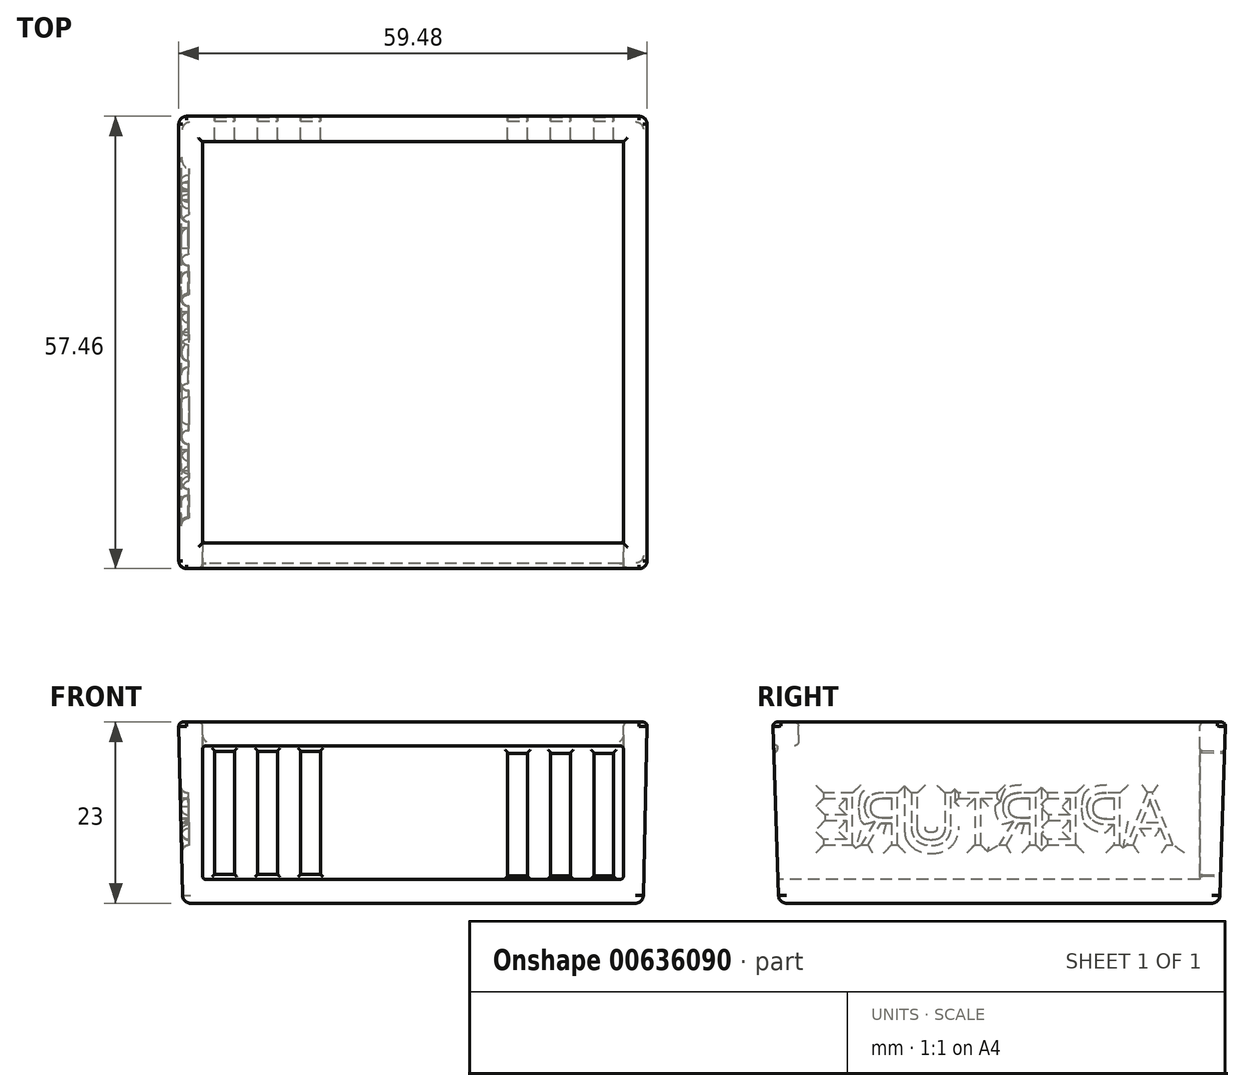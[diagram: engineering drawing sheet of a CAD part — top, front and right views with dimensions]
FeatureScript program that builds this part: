
annotation { "Feature Type Name" : "Feature", "Feature Type Description" : "" }
export const myFeature = defineFeature(function(context is Context, id is Id, definition is map)
    precondition{}
    {
        {
            var Q0;
            Q0=qCreatedBy(makeId("Top.planeOp"),FACE);
            var sketch = newSketch(context, id + "F0", { "sketchPlane" : qUnion([Q0])});
            skLineSegment(sketch, "E0.bottom", {"start": v(29.25, 28) * mm, "end": v(-29.25, 28) * mm});
            skLineSegment(sketch, "E0.top", {"start": v(29.25, -28) * mm, "end": v(-29.25, -28) * mm});
            skLineSegment(sketch, "E0.left", {"start": v(29.25, 28) * mm, "end": v(29.25, -28) * mm});
            skLineSegment(sketch, "E0.right", {"start": v(-29.25, 28) * mm, "end": v(-29.25, -28) * mm});
            skPoint(sketch, "E0.middle", {"position": v(0, 0) * mm});
            skSolve(sketch);
        }
        {
            var Q0;
            Q0=qCreatedBy(makeId("Top.planeOp"),FACE);
            cPlane(context, id + "F1", {"entities" : qUnion([Q0]), "cplaneType" : CPlaneType.OFFSET, "offset" : 23 * mm, "width" : 150 * mm, "height" : 150 * mm});
        }
        {
            var Q0;
            Q0=qCreatedBy(id+"F1.planeOp",FACE);
            var sketch = newSketch(context, id + "F2", { "sketchPlane" : qUnion([Q0])});
            skLineSegment(sketch, "E1.bottom", {"start": v(29.75, 28.75) * mm, "end": v(-29.75, 28.75) * mm});
            skLineSegment(sketch, "E1.top", {"start": v(29.75, -28.75) * mm, "end": v(-29.75, -28.75) * mm});
            skLineSegment(sketch, "E1.left", {"start": v(29.75, 28.75) * mm, "end": v(29.75, -28.75) * mm});
            skLineSegment(sketch, "E1.right", {"start": v(-29.75, 28.75) * mm, "end": v(-29.75, -28.75) * mm});
            skPoint(sketch, "E1.middle", {"position": v(0, 0) * mm});
            skSolve(sketch);
        }
        {
            var Q0;
            Q0=makeQuery(id+"F0.imprint","IMPRINT",FACE,{"disambiguationData":[TD([[makeQuery(id+"F0.imprint","IMPRINT",EDGE,{"derivedFrom":sQuery(id+"F0.wireOp",EDGE,"E0.bottom")}),1.0]])]});
            var Q1;
            Q1=makeQuery(id+"F2.imprint","IMPRINT",FACE,{"disambiguationData":[TD([[makeQuery(id+"F2.imprint","IMPRINT",EDGE,{"derivedFrom":sQuery(id+"F2.wireOp",EDGE,"E1.bottom")}),1.0]])]});
            loft(context, id + "F3", {"sheetProfilesArray" : [{ "sheetProfileEntities" : qUnion([Q0]) }, { "sheetProfileEntities" : qUnion([Q1]) }]});
        }
        {
            var Q0;
            Q0=qCreatedBy(id+"F1.planeOp",FACE);
            var sketch = newSketch(context, id + "F4", { "sketchPlane" : qUnion([Q0])});
            skLineSegment(sketch, "E2.bottom", {"start": v(26.75, 25.5) * mm, "end": v(-26.75, 25.5) * mm});
            skLineSegment(sketch, "E2.top", {"start": v(26.75, -25.5) * mm, "end": v(-26.75, -25.5) * mm});
            skLineSegment(sketch, "E2.left", {"start": v(26.75, 25.5) * mm, "end": v(26.75, -25.5) * mm});
            skLineSegment(sketch, "E2.right", {"start": v(-26.75, 25.5) * mm, "end": v(-26.75, -25.5) * mm});
            skPoint(sketch, "E2.middle", {"position": v(0, 0) * mm});
            skSolve(sketch);
        }
        {
            var Q0;
            Q0=makeQuery(id+"F4.imprint","IMPRINT",FACE,{"disambiguationData":[TD([[makeQuery(id+"F4.imprint","IMPRINT",EDGE,{"derivedFrom":sQuery(id+"F4.wireOp",EDGE,"E2.bottom")}),1.0]])]});
            extrude(context, id + "F5", {"entities" : qUnion([Q0]), "operationType" : NewBodyOperationType.REMOVE, "oppositeDirection" : true, "depth" : 20 * mm, "offsetDistance" : 25 * mm});
        }
        {
            var Q0;
            Q0=makeQuery(id+"F3.opLoft","SWEPT_FACE",FACE,{"disambiguationData":[OSD([sQuery(id+"F0.wireOp",EDGE,"E0.bottom"),sQuery(id+"F0.wireOp",EDGE,"E0.left"),sQuery(id+"F0.wireOp",EDGE,"E0.right"),sQuery(id+"F2.wireOp",EDGE,"E1.bottom"),sQuery(id+"F2.wireOp",EDGE,"E1.left"),sQuery(id+"F2.wireOp",EDGE,"E1.right")])]});
            cPlane(context, id + "F6", {"entities" : qUnion([Q0]), "cplaneType" : CPlaneType.OFFSET, "offset" : 0 * mm, "width" : 150 * mm, "height" : 150 * mm});
        }
        {
            var Q0;
            Q0=qCreatedBy(id+"F6.planeOp",FACE);
            var sketch = newSketch(context, id + "F7", { "sketchPlane" : qUnion([Q0])});
            skLineSegment(sketch, "E3.bottom", {"start": v(-22.97, 19.97) * mm, "end": v(-25.49, 19.97) * mm});
            skLineSegment(sketch, "E3.top", {"start": v(-22.97, 4.28) * mm, "end": v(-25.49, 4.28) * mm});
            skLineSegment(sketch, "E3.left", {"start": v(-22.97, 19.97) * mm, "end": v(-22.97, 4.28) * mm});
            skLineSegment(sketch, "E3.right", {"start": v(-25.49, 19.97) * mm, "end": v(-25.49, 4.28) * mm});
            skPoint(sketch, "E3.middle", {"position": v(-24.23, 12.13) * mm});
            skLineSegment(sketch, "E4.bottom", {"start": v(-17.5, 19.97) * mm, "end": v(-20.03, 19.97) * mm});
            skLineSegment(sketch, "E4.top", {"start": v(-17.5, 4.28) * mm, "end": v(-20.03, 4.28) * mm});
            skLineSegment(sketch, "E4.left", {"start": v(-17.5, 19.97) * mm, "end": v(-17.5, 4.28) * mm});
            skLineSegment(sketch, "E4.right", {"start": v(-20.03, 19.97) * mm, "end": v(-20.03, 4.28) * mm});
            skPoint(sketch, "E4.middle", {"position": v(-18.76, 12.13) * mm});
            skLineSegment(sketch, "E5.bottom", {"start": v(-12.04, 19.97) * mm, "end": v(-14.56, 19.97) * mm});
            skLineSegment(sketch, "E5.top", {"start": v(-12.04, 4.28) * mm, "end": v(-14.56, 4.28) * mm});
            skLineSegment(sketch, "E5.left", {"start": v(-12.04, 19.97) * mm, "end": v(-12.04, 4.28) * mm});
            skLineSegment(sketch, "E5.right", {"start": v(-14.56, 19.97) * mm, "end": v(-14.56, 4.28) * mm});
            skPoint(sketch, "E5.middle", {"position": v(-13.3, 12.13) * mm});
            skLineSegment(sketch, "E6.bottom", {"start": v(14.27, 20.2) * mm, "end": v(11.75, 20.2) * mm});
            skLineSegment(sketch, "E6.top", {"start": v(14.27, 4.5) * mm, "end": v(11.75, 4.5) * mm});
            skLineSegment(sketch, "E6.left", {"start": v(14.27, 20.2) * mm, "end": v(14.27, 4.5) * mm});
            skLineSegment(sketch, "E6.right", {"start": v(11.75, 20.2) * mm, "end": v(11.75, 4.5) * mm});
            skPoint(sketch, "E6.middle", {"position": v(13, 12.36) * mm});
            skLineSegment(sketch, "E7.bottom", {"start": v(19.73, 20.2) * mm, "end": v(17.21, 20.2) * mm});
            skLineSegment(sketch, "E7.top", {"start": v(19.73, 4.5) * mm, "end": v(17.21, 4.5) * mm});
            skLineSegment(sketch, "E7.left", {"start": v(19.73, 20.2) * mm, "end": v(19.73, 4.5) * mm});
            skLineSegment(sketch, "E7.right", {"start": v(17.21, 20.2) * mm, "end": v(17.21, 4.5) * mm});
            skPoint(sketch, "E7.middle", {"position": v(18.47, 12.36) * mm});
            skLineSegment(sketch, "E8.bottom", {"start": v(25.2, 20.2) * mm, "end": v(22.67, 20.2) * mm});
            skLineSegment(sketch, "E8.top", {"start": v(25.2, 4.5) * mm, "end": v(22.67, 4.5) * mm});
            skLineSegment(sketch, "E8.left", {"start": v(25.2, 20.2) * mm, "end": v(25.2, 4.5) * mm});
            skLineSegment(sketch, "E8.right", {"start": v(22.67, 20.2) * mm, "end": v(22.67, 4.5) * mm});
            skPoint(sketch, "E8.middle", {"position": v(23.94, 12.36) * mm});
            skSolve(sketch);
        }
        {
            var Q0;
            Q0 = qSketchRegion(id + "F7", true);
            extrude(context, id + "F8", {"entities" : qUnion([Q0]), "operationType" : NewBodyOperationType.REMOVE, "oppositeDirection" : true, "depth" : 5 * mm, "offsetDistance" : 25 * mm});
        }
        {
            var Q0;
            Q0=makeQuery(id+"F5.boolean.opBoolean","COPY",FACE,{"derivedFrom":makeQuery(id+"F5.opExtrude","SWEPT_FACE",FACE,{"disambiguationData":[OSD([sQuery(id+"F4.wireOp",EDGE,"E2.top")])]})});
            var sketch = newSketch(context, id + "F9", { "sketchPlane" : qUnion([Q0])});
            skPoint(sketch, "E9", {"position": v(-26.75, 20) * mm});
            skPoint(sketch, "E10", {"position": v(26.75, 20) * mm});
            skPoint(sketch, "E11", {"position": v(26.75, 3) * mm});
            skPoint(sketch, "E12", {"position": v(-26.75, 3) * mm});
            skLineSegment(sketch, "E13", {"start": v(-26.75, 20) * mm, "end": v(-26.75, 3) * mm});
            skLineSegment(sketch, "E14", {"start": v(-26.75, 20) * mm, "end": v(26.75, 20) * mm});
            skLineSegment(sketch, "E15", {"start": v(26.75, 20) * mm, "end": v(26.75, 3) * mm});
            skLineSegment(sketch, "E16", {"start": v(26.75, 3) * mm, "end": v(-26.75, 3) * mm});
            skSolve(sketch);
        }
        {
            var Q0;
            Q0=makeQuery(id+"F9.imprint","IMPRINT",FACE,{"disambiguationData":[TD([[makeQuery(id+"F9.imprint","IMPRINT",EDGE,{"derivedFrom":sQuery(id+"F9.wireOp",EDGE,"E13")}),-1.0]])]});
            extrude(context, id + "F10", {"entities" : qUnion([Q0]), "operationType" : NewBodyOperationType.REMOVE, "oppositeDirection" : true, "depth" : 25 * mm, "offsetDistance" : 25 * mm});
        }
        {
            var Q0;
            Q0=makeQuery(id+"F3.opLoft","SWEPT_FACE",FACE,{"disambiguationData":[OSD([sQuery(id+"F0.wireOp",EDGE,"E0.bottom"),sQuery(id+"F0.wireOp",EDGE,"E0.top"),sQuery(id+"F0.wireOp",EDGE,"E0.right"),sQuery(id+"F2.wireOp",EDGE,"E1.bottom"),sQuery(id+"F2.wireOp",EDGE,"E1.top"),sQuery(id+"F2.wireOp",EDGE,"E1.right")])]});
            var sketch = newSketch(context, id + "F11", { "sketchPlane" : qUnion([Q0])});
            skText(sketch, "E17", { "text": "APERTURE\n", "fontName": "OpenSans-Regular.ttf"});
            const initialGuessF11  = {"E17": [-0.02208, 0.00804, 1, 0, 0.00665]};
            skSetInitialGuess(sketch, initialGuessF11);
            skSolve(sketch);
        }
        {
            var Q0;
            Q0 = qSketchRegion(id + "F11", true);
            extrude(context, id + "F12", {"entities" : qUnion([Q0]), "operationType" : NewBodyOperationType.REMOVE, "oppositeDirection" : true, "depth" : 1 * mm, "offsetDistance" : 25 * mm});
        }
        {
            var Q0;
            Q0=makeQuery(id+"F10.boolean.opBoolean","MERGE",EDGE,{"derivedFrom":[makeQuery(id+"F5.boolean.opBoolean","COPY",EDGE,{"derivedFrom":makeQuery(id+"F5.opExtrude","CAP_EDGE",EDGE,{"disambiguationData":[OSD([sQuery(id+"F4.wireOp",EDGE,"E2.right")])],"isStart":false})}),makeQuery(id+"F10.opExtrude","SWEPT_EDGE",EDGE,{"disambiguationData":[OSD([sQuery(id+"F9.wireOp",EDGE,"E15"),sQuery(id+"F9.wireOp",EDGE,"E16")])]})]});
            var Q1;
            Q1=makeQuery(id+"F10.boolean.opBoolean","INTERSECT",EDGE,{"derivedFrom":[makeQuery(id+"F3.opLoft","SWEPT_FACE",FACE,{"disambiguationData":[OSD([sQuery(id+"F0.wireOp",EDGE,"E0.top"),sQuery(id+"F0.wireOp",EDGE,"E0.left"),sQuery(id+"F0.wireOp",EDGE,"E0.right"),sQuery(id+"F2.wireOp",EDGE,"E1.top"),sQuery(id+"F2.wireOp",EDGE,"E1.left"),sQuery(id+"F2.wireOp",EDGE,"E1.right")])]}),makeQuery(id+"F10.opExtrude","SWEPT_FACE",FACE,{"disambiguationData":[OSD([sQuery(id+"F9.wireOp",EDGE,"E14")])]})]});
            var Q2;
            Q2=makeQuery(id+"F10.boolean.opBoolean","COPY",FACE,{"derivedFrom":makeQuery(id+"F10.opExtrude","SWEPT_FACE",FACE,{"disambiguationData":[OSD([sQuery(id+"F9.wireOp",EDGE,"E14")])]})});
            var Q3;
            Q3=makeQuery(id+"F3.opLoft","CAP_FACE",FACE,{"disambiguationData":[OSD([makeQuery(id+"F2.imprint","IMPRINT",FACE,{"disambiguationData":[TD([[makeQuery(id+"F2.imprint","IMPRINT",EDGE,{"derivedFrom":sQuery(id+"F2.wireOp",EDGE,"E1.bottom")}),1.0]])]})])],"isStart":true});
            fillet(context, id + "F13", {"entities" : qUnion([Q0, Q1, Q2, Q3]), "radius" : .5 * mm, "tangentPropagation" : true, "allowEdgeOverflow" : false});
        }
        {
            var Q0;
            Q0=makeQuery(id+"F3.opLoft","CAP_FACE",FACE,{"disambiguationData":[OSD([makeQuery(id+"F0.imprint","IMPRINT",FACE,{"disambiguationData":[TD([[makeQuery(id+"F0.imprint","IMPRINT",EDGE,{"derivedFrom":sQuery(id+"F0.wireOp",EDGE,"E0.bottom")}),1.0]])]})])],"isStart":true});
            var Q1;
            Q1=makeQuery(id+"F3.opLoft","SWEPT_FACE",FACE,{"disambiguationData":[OSD([sQuery(id+"F0.wireOp",EDGE,"E0.bottom"),sQuery(id+"F0.wireOp",EDGE,"E0.top"),sQuery(id+"F0.wireOp",EDGE,"E0.left"),sQuery(id+"F2.wireOp",EDGE,"E1.bottom"),sQuery(id+"F2.wireOp",EDGE,"E1.top"),sQuery(id+"F2.wireOp",EDGE,"E1.left")])]});
            var Q2;
            {var subQ0=sQuery(id+"F2.wireOp",EDGE,"E1.right");var subQ2=sQuery(id+"F2.wireOp",EDGE,"E1.bottom");var subQ3=sQuery(id+"F0.wireOp",EDGE,"E0.right");var subQ5=sQuery(id+"F0.wireOp",EDGE,"E0.bottom");var subQ6=sQuery(id+"F2.wireOp",EDGE,"E1.top");var subQ7=sQuery(id+"F0.wireOp",EDGE,"E0.top");Q2=makeQuery(id+"F12.boolean.opBoolean","SPLIT",FACE,{"disambiguationData":[TD([makeQuery(id+"F12.opExtrude","SWEPT_FACE",FACE,{"disambiguationData":[OSD([sQuery(id+"F11.wireOp",EDGE,"E17.sketch_text.stroke-0")])]})])],"derivedFrom":makeQuery(id+"F3.opLoft","SWEPT_FACE",FACE,{"disambiguationData":[OSD([subQ5,subQ7,subQ3,subQ2,subQ6,subQ0])]})});}
            fillet(context, id + "F14", {"entities" : qUnion([Q0, Q1, Q2]), "radius" : 1 * mm, "tangentPropagation" : true, "allowEdgeOverflow" : false});
        }
        {
            var Q0;
            Q0=makeQuery(id+"F8.boolean.opBoolean","INTERSECT",EDGE,{"derivedFrom":[makeQuery(id+"F5.boolean.opBoolean","COPY",FACE,{"derivedFrom":makeQuery(id+"F5.opExtrude","SWEPT_FACE",FACE,{"disambiguationData":[OSD([sQuery(id+"F4.wireOp",EDGE,"E2.bottom")])]})}),makeQuery(id+"F8.opExtrude","SWEPT_FACE",FACE,{"disambiguationData":[OSD([sQuery(id+"F7.wireOp",EDGE,"E3.right")])]})]});
            var Q1;
            Q1=makeQuery(id+"F8.boolean.opBoolean","COPY",EDGE,{"derivedFrom":makeQuery(id+"F8.opExtrude","CAP_EDGE",EDGE,{"disambiguationData":[OSD([sQuery(id+"F7.wireOp",EDGE,"E3.right")])],"isStart":true})});
            var Q2;
            Q2=makeQuery(id+"F8.boolean.opBoolean","INTERSECT",EDGE,{"derivedFrom":[makeQuery(id+"F5.boolean.opBoolean","COPY",FACE,{"derivedFrom":makeQuery(id+"F5.opExtrude","SWEPT_FACE",FACE,{"disambiguationData":[OSD([sQuery(id+"F4.wireOp",EDGE,"E2.bottom")])]})}),makeQuery(id+"F8.opExtrude","SWEPT_FACE",FACE,{"disambiguationData":[OSD([sQuery(id+"F7.wireOp",EDGE,"E3.top")])]})]});
            var Q3;
            Q3=makeQuery(id+"F8.boolean.opBoolean","COPY",EDGE,{"derivedFrom":makeQuery(id+"F8.opExtrude","CAP_EDGE",EDGE,{"disambiguationData":[OSD([sQuery(id+"F7.wireOp",EDGE,"E3.top")])],"isStart":true})});
            var Q4;
            Q4=makeQuery(id+"F8.boolean.opBoolean","COPY",EDGE,{"derivedFrom":makeQuery(id+"F8.opExtrude","CAP_EDGE",EDGE,{"disambiguationData":[OSD([sQuery(id+"F7.wireOp",EDGE,"E3.left")])],"isStart":true})});
            var Q5;
            Q5=makeQuery(id+"F8.boolean.opBoolean","INTERSECT",EDGE,{"derivedFrom":[makeQuery(id+"F5.boolean.opBoolean","COPY",FACE,{"derivedFrom":makeQuery(id+"F5.opExtrude","SWEPT_FACE",FACE,{"disambiguationData":[OSD([sQuery(id+"F4.wireOp",EDGE,"E2.bottom")])]})}),makeQuery(id+"F8.opExtrude","SWEPT_FACE",FACE,{"disambiguationData":[OSD([sQuery(id+"F7.wireOp",EDGE,"E3.left")])]})]});
            var Q6;
            Q6=makeQuery(id+"F8.boolean.opBoolean","COPY",EDGE,{"derivedFrom":makeQuery(id+"F8.opExtrude","CAP_EDGE",EDGE,{"disambiguationData":[OSD([sQuery(id+"F7.wireOp",EDGE,"E3.bottom")])],"isStart":true})});
            var Q7;
            Q7=makeQuery(id+"F8.boolean.opBoolean","INTERSECT",EDGE,{"derivedFrom":[makeQuery(id+"F5.boolean.opBoolean","COPY",FACE,{"derivedFrom":makeQuery(id+"F5.opExtrude","SWEPT_FACE",FACE,{"disambiguationData":[OSD([sQuery(id+"F4.wireOp",EDGE,"E2.bottom")])]})}),makeQuery(id+"F8.opExtrude","SWEPT_FACE",FACE,{"disambiguationData":[OSD([sQuery(id+"F7.wireOp",EDGE,"E3.bottom")])]})]});
            var Q8;
            Q8=makeQuery(id+"F8.boolean.opBoolean","COPY",EDGE,{"derivedFrom":makeQuery(id+"F8.opExtrude","CAP_EDGE",EDGE,{"disambiguationData":[OSD([sQuery(id+"F7.wireOp",EDGE,"E4.left")])],"isStart":true})});
            var Q9;
            Q9=makeQuery(id+"F8.boolean.opBoolean","INTERSECT",EDGE,{"derivedFrom":[makeQuery(id+"F5.boolean.opBoolean","COPY",FACE,{"derivedFrom":makeQuery(id+"F5.opExtrude","SWEPT_FACE",FACE,{"disambiguationData":[OSD([sQuery(id+"F4.wireOp",EDGE,"E2.bottom")])]})}),makeQuery(id+"F8.opExtrude","SWEPT_FACE",FACE,{"disambiguationData":[OSD([sQuery(id+"F7.wireOp",EDGE,"E4.bottom")])]})]});
            var Q10;
            Q10=makeQuery(id+"F8.boolean.opBoolean","COPY",EDGE,{"derivedFrom":makeQuery(id+"F8.opExtrude","CAP_EDGE",EDGE,{"disambiguationData":[OSD([sQuery(id+"F7.wireOp",EDGE,"E4.bottom")])],"isStart":true})});
            var Q11;
            Q11=makeQuery(id+"F8.boolean.opBoolean","COPY",EDGE,{"derivedFrom":makeQuery(id+"F8.opExtrude","CAP_EDGE",EDGE,{"disambiguationData":[OSD([sQuery(id+"F7.wireOp",EDGE,"E5.bottom")])],"isStart":true})});
            var Q12;
            Q12=makeQuery(id+"F8.boolean.opBoolean","COPY",EDGE,{"derivedFrom":makeQuery(id+"F8.opExtrude","CAP_EDGE",EDGE,{"disambiguationData":[OSD([sQuery(id+"F7.wireOp",EDGE,"E5.left")])],"isStart":true})});
            var Q13;
            Q13=makeQuery(id+"F8.boolean.opBoolean","INTERSECT",EDGE,{"derivedFrom":[makeQuery(id+"F5.boolean.opBoolean","COPY",FACE,{"derivedFrom":makeQuery(id+"F5.opExtrude","SWEPT_FACE",FACE,{"disambiguationData":[OSD([sQuery(id+"F4.wireOp",EDGE,"E2.bottom")])]})}),makeQuery(id+"F8.opExtrude","SWEPT_FACE",FACE,{"disambiguationData":[OSD([sQuery(id+"F7.wireOp",EDGE,"E5.left")])]})]});
            var Q14;
            Q14=makeQuery(id+"F8.boolean.opBoolean","COPY",EDGE,{"derivedFrom":makeQuery(id+"F8.opExtrude","CAP_EDGE",EDGE,{"disambiguationData":[OSD([sQuery(id+"F7.wireOp",EDGE,"E4.right")])],"isStart":true})});
            var Q15;
            Q15=makeQuery(id+"F8.boolean.opBoolean","INTERSECT",EDGE,{"derivedFrom":[makeQuery(id+"F5.boolean.opBoolean","COPY",FACE,{"derivedFrom":makeQuery(id+"F5.opExtrude","SWEPT_FACE",FACE,{"disambiguationData":[OSD([sQuery(id+"F4.wireOp",EDGE,"E2.bottom")])]})}),makeQuery(id+"F8.opExtrude","SWEPT_FACE",FACE,{"disambiguationData":[OSD([sQuery(id+"F7.wireOp",EDGE,"E4.left")])]})]});
            var Q16;
            Q16=makeQuery(id+"F8.boolean.opBoolean","COPY",EDGE,{"derivedFrom":makeQuery(id+"F8.opExtrude","CAP_EDGE",EDGE,{"disambiguationData":[OSD([sQuery(id+"F7.wireOp",EDGE,"E4.top")])],"isStart":true})});
            var Q17;
            Q17=makeQuery(id+"F8.boolean.opBoolean","INTERSECT",EDGE,{"derivedFrom":[makeQuery(id+"F5.boolean.opBoolean","COPY",FACE,{"derivedFrom":makeQuery(id+"F5.opExtrude","SWEPT_FACE",FACE,{"disambiguationData":[OSD([sQuery(id+"F4.wireOp",EDGE,"E2.bottom")])]})}),makeQuery(id+"F8.opExtrude","SWEPT_FACE",FACE,{"disambiguationData":[OSD([sQuery(id+"F7.wireOp",EDGE,"E4.top")])]})]});
            var Q18;
            Q18=makeQuery(id+"F8.boolean.opBoolean","INTERSECT",EDGE,{"derivedFrom":[makeQuery(id+"F5.boolean.opBoolean","COPY",FACE,{"derivedFrom":makeQuery(id+"F5.opExtrude","SWEPT_FACE",FACE,{"disambiguationData":[OSD([sQuery(id+"F4.wireOp",EDGE,"E2.bottom")])]})}),makeQuery(id+"F8.opExtrude","SWEPT_FACE",FACE,{"disambiguationData":[OSD([sQuery(id+"F7.wireOp",EDGE,"E4.right")])]})]});
            var Q19;
            Q19=makeQuery(id+"F8.boolean.opBoolean","INTERSECT",EDGE,{"derivedFrom":[makeQuery(id+"F5.boolean.opBoolean","COPY",FACE,{"derivedFrom":makeQuery(id+"F5.opExtrude","SWEPT_FACE",FACE,{"disambiguationData":[OSD([sQuery(id+"F4.wireOp",EDGE,"E2.bottom")])]})}),makeQuery(id+"F8.opExtrude","SWEPT_FACE",FACE,{"disambiguationData":[OSD([sQuery(id+"F7.wireOp",EDGE,"E5.right")])]})]});
            var Q20;
            Q20=makeQuery(id+"F8.boolean.opBoolean","COPY",EDGE,{"derivedFrom":makeQuery(id+"F8.opExtrude","CAP_EDGE",EDGE,{"disambiguationData":[OSD([sQuery(id+"F7.wireOp",EDGE,"E5.right")])],"isStart":true})});
            var Q21;
            Q21=makeQuery(id+"F8.boolean.opBoolean","COPY",EDGE,{"derivedFrom":makeQuery(id+"F8.opExtrude","CAP_EDGE",EDGE,{"disambiguationData":[OSD([sQuery(id+"F7.wireOp",EDGE,"E5.top")])],"isStart":true})});
            var Q22;
            Q22=makeQuery(id+"F8.boolean.opBoolean","INTERSECT",EDGE,{"derivedFrom":[makeQuery(id+"F5.boolean.opBoolean","COPY",FACE,{"derivedFrom":makeQuery(id+"F5.opExtrude","SWEPT_FACE",FACE,{"disambiguationData":[OSD([sQuery(id+"F4.wireOp",EDGE,"E2.bottom")])]})}),makeQuery(id+"F8.opExtrude","SWEPT_FACE",FACE,{"disambiguationData":[OSD([sQuery(id+"F7.wireOp",EDGE,"E5.bottom")])]})]});
            var Q23;
            Q23=makeQuery(id+"F8.boolean.opBoolean","INTERSECT",EDGE,{"derivedFrom":[makeQuery(id+"F5.boolean.opBoolean","COPY",FACE,{"derivedFrom":makeQuery(id+"F5.opExtrude","SWEPT_FACE",FACE,{"disambiguationData":[OSD([sQuery(id+"F4.wireOp",EDGE,"E2.bottom")])]})}),makeQuery(id+"F8.opExtrude","SWEPT_FACE",FACE,{"disambiguationData":[OSD([sQuery(id+"F7.wireOp",EDGE,"E5.top")])]})]});
            var Q24;
            Q24=makeQuery(id+"F8.boolean.opBoolean","INTERSECT",EDGE,{"derivedFrom":[makeQuery(id+"F5.boolean.opBoolean","COPY",FACE,{"derivedFrom":makeQuery(id+"F5.opExtrude","SWEPT_FACE",FACE,{"disambiguationData":[OSD([sQuery(id+"F4.wireOp",EDGE,"E2.bottom")])]})}),makeQuery(id+"F8.opExtrude","SWEPT_FACE",FACE,{"disambiguationData":[OSD([sQuery(id+"F7.wireOp",EDGE,"E8.top")])]})]});
            var Q25;
            Q25=makeQuery(id+"F8.boolean.opBoolean","INTERSECT",EDGE,{"derivedFrom":[makeQuery(id+"F5.boolean.opBoolean","COPY",FACE,{"derivedFrom":makeQuery(id+"F5.opExtrude","SWEPT_FACE",FACE,{"disambiguationData":[OSD([sQuery(id+"F4.wireOp",EDGE,"E2.bottom")])]})}),makeQuery(id+"F8.opExtrude","SWEPT_FACE",FACE,{"disambiguationData":[OSD([sQuery(id+"F7.wireOp",EDGE,"E7.top")])]})]});
            var Q26;
            Q26=makeQuery(id+"F8.boolean.opBoolean","INTERSECT",EDGE,{"derivedFrom":[makeQuery(id+"F5.boolean.opBoolean","COPY",FACE,{"derivedFrom":makeQuery(id+"F5.opExtrude","SWEPT_FACE",FACE,{"disambiguationData":[OSD([sQuery(id+"F4.wireOp",EDGE,"E2.bottom")])]})}),makeQuery(id+"F8.opExtrude","SWEPT_FACE",FACE,{"disambiguationData":[OSD([sQuery(id+"F7.wireOp",EDGE,"E6.top")])]})]});
            var Q27;
            Q27=makeQuery(id+"F8.boolean.opBoolean","COPY",EDGE,{"derivedFrom":makeQuery(id+"F8.opExtrude","CAP_EDGE",EDGE,{"disambiguationData":[OSD([sQuery(id+"F7.wireOp",EDGE,"E6.top")])],"isStart":true})});
            var Q28;
            Q28=makeQuery(id+"F8.boolean.opBoolean","COPY",EDGE,{"derivedFrom":makeQuery(id+"F8.opExtrude","CAP_EDGE",EDGE,{"disambiguationData":[OSD([sQuery(id+"F7.wireOp",EDGE,"E7.top")])],"isStart":true})});
            var Q29;
            Q29=makeQuery(id+"F8.boolean.opBoolean","COPY",EDGE,{"derivedFrom":makeQuery(id+"F8.opExtrude","CAP_EDGE",EDGE,{"disambiguationData":[OSD([sQuery(id+"F7.wireOp",EDGE,"E8.top")])],"isStart":true})});
            var Q30;
            Q30=makeQuery(id+"F8.boolean.opBoolean","INTERSECT",EDGE,{"derivedFrom":[makeQuery(id+"F5.boolean.opBoolean","COPY",FACE,{"derivedFrom":makeQuery(id+"F5.opExtrude","SWEPT_FACE",FACE,{"disambiguationData":[OSD([sQuery(id+"F4.wireOp",EDGE,"E2.bottom")])]})}),makeQuery(id+"F8.opExtrude","SWEPT_FACE",FACE,{"disambiguationData":[OSD([sQuery(id+"F7.wireOp",EDGE,"E8.left")])]})]});
            var Q31;
            Q31=makeQuery(id+"F8.boolean.opBoolean","INTERSECT",EDGE,{"derivedFrom":[makeQuery(id+"F5.boolean.opBoolean","COPY",FACE,{"derivedFrom":makeQuery(id+"F5.opExtrude","SWEPT_FACE",FACE,{"disambiguationData":[OSD([sQuery(id+"F4.wireOp",EDGE,"E2.bottom")])]})}),makeQuery(id+"F8.opExtrude","SWEPT_FACE",FACE,{"disambiguationData":[OSD([sQuery(id+"F7.wireOp",EDGE,"E8.right")])]})]});
            var Q32;
            Q32=makeQuery(id+"F8.boolean.opBoolean","INTERSECT",EDGE,{"derivedFrom":[makeQuery(id+"F5.boolean.opBoolean","COPY",FACE,{"derivedFrom":makeQuery(id+"F5.opExtrude","SWEPT_FACE",FACE,{"disambiguationData":[OSD([sQuery(id+"F4.wireOp",EDGE,"E2.bottom")])]})}),makeQuery(id+"F8.opExtrude","SWEPT_FACE",FACE,{"disambiguationData":[OSD([sQuery(id+"F7.wireOp",EDGE,"E7.left")])]})]});
            var Q33;
            Q33=makeQuery(id+"F8.boolean.opBoolean","INTERSECT",EDGE,{"derivedFrom":[makeQuery(id+"F5.boolean.opBoolean","COPY",FACE,{"derivedFrom":makeQuery(id+"F5.opExtrude","SWEPT_FACE",FACE,{"disambiguationData":[OSD([sQuery(id+"F4.wireOp",EDGE,"E2.bottom")])]})}),makeQuery(id+"F8.opExtrude","SWEPT_FACE",FACE,{"disambiguationData":[OSD([sQuery(id+"F7.wireOp",EDGE,"E6.left")])]})]});
            var Q34;
            Q34=makeQuery(id+"F8.boolean.opBoolean","INTERSECT",EDGE,{"derivedFrom":[makeQuery(id+"F5.boolean.opBoolean","COPY",FACE,{"derivedFrom":makeQuery(id+"F5.opExtrude","SWEPT_FACE",FACE,{"disambiguationData":[OSD([sQuery(id+"F4.wireOp",EDGE,"E2.bottom")])]})}),makeQuery(id+"F8.opExtrude","SWEPT_FACE",FACE,{"disambiguationData":[OSD([sQuery(id+"F7.wireOp",EDGE,"E6.right")])]})]});
            var Q35;
            Q35=makeQuery(id+"F8.boolean.opBoolean","INTERSECT",EDGE,{"derivedFrom":[makeQuery(id+"F5.boolean.opBoolean","COPY",FACE,{"derivedFrom":makeQuery(id+"F5.opExtrude","SWEPT_FACE",FACE,{"disambiguationData":[OSD([sQuery(id+"F4.wireOp",EDGE,"E2.bottom")])]})}),makeQuery(id+"F8.opExtrude","SWEPT_FACE",FACE,{"disambiguationData":[OSD([sQuery(id+"F7.wireOp",EDGE,"E7.right")])]})]});
            var Q36;
            Q36=makeQuery(id+"F8.boolean.opBoolean","INTERSECT",EDGE,{"derivedFrom":[makeQuery(id+"F5.boolean.opBoolean","COPY",FACE,{"derivedFrom":makeQuery(id+"F5.opExtrude","SWEPT_FACE",FACE,{"disambiguationData":[OSD([sQuery(id+"F4.wireOp",EDGE,"E2.bottom")])]})}),makeQuery(id+"F8.opExtrude","SWEPT_FACE",FACE,{"disambiguationData":[OSD([sQuery(id+"F7.wireOp",EDGE,"E6.bottom")])]})]});
            var Q37;
            Q37=makeQuery(id+"F8.boolean.opBoolean","COPY",EDGE,{"derivedFrom":makeQuery(id+"F8.opExtrude","CAP_EDGE",EDGE,{"disambiguationData":[OSD([sQuery(id+"F7.wireOp",EDGE,"E6.bottom")])],"isStart":true})});
            var Q38;
            Q38=makeQuery(id+"F8.boolean.opBoolean","INTERSECT",EDGE,{"derivedFrom":[makeQuery(id+"F5.boolean.opBoolean","COPY",FACE,{"derivedFrom":makeQuery(id+"F5.opExtrude","SWEPT_FACE",FACE,{"disambiguationData":[OSD([sQuery(id+"F4.wireOp",EDGE,"E2.bottom")])]})}),makeQuery(id+"F8.opExtrude","SWEPT_FACE",FACE,{"disambiguationData":[OSD([sQuery(id+"F7.wireOp",EDGE,"E7.bottom")])]})]});
            var Q39;
            Q39=makeQuery(id+"F8.boolean.opBoolean","COPY",EDGE,{"derivedFrom":makeQuery(id+"F8.opExtrude","CAP_EDGE",EDGE,{"disambiguationData":[OSD([sQuery(id+"F7.wireOp",EDGE,"E7.bottom")])],"isStart":true})});
            var Q40;
            Q40=makeQuery(id+"F8.boolean.opBoolean","INTERSECT",EDGE,{"derivedFrom":[makeQuery(id+"F5.boolean.opBoolean","COPY",FACE,{"derivedFrom":makeQuery(id+"F5.opExtrude","SWEPT_FACE",FACE,{"disambiguationData":[OSD([sQuery(id+"F4.wireOp",EDGE,"E2.bottom")])]})}),makeQuery(id+"F8.opExtrude","SWEPT_FACE",FACE,{"disambiguationData":[OSD([sQuery(id+"F7.wireOp",EDGE,"E8.bottom")])]})]});
            var Q41;
            Q41=makeQuery(id+"F8.boolean.opBoolean","COPY",EDGE,{"derivedFrom":makeQuery(id+"F8.opExtrude","CAP_EDGE",EDGE,{"disambiguationData":[OSD([sQuery(id+"F7.wireOp",EDGE,"E8.bottom")])],"isStart":true})});
            var Q42;
            Q42=makeQuery(id+"F8.boolean.opBoolean","COPY",EDGE,{"derivedFrom":makeQuery(id+"F8.opExtrude","CAP_EDGE",EDGE,{"disambiguationData":[OSD([sQuery(id+"F7.wireOp",EDGE,"E6.right")])],"isStart":true})});
            var Q43;
            Q43=makeQuery(id+"F8.boolean.opBoolean","COPY",EDGE,{"derivedFrom":makeQuery(id+"F8.opExtrude","CAP_EDGE",EDGE,{"disambiguationData":[OSD([sQuery(id+"F7.wireOp",EDGE,"E6.left")])],"isStart":true})});
            var Q44;
            Q44=makeQuery(id+"F8.boolean.opBoolean","COPY",EDGE,{"derivedFrom":makeQuery(id+"F8.opExtrude","CAP_EDGE",EDGE,{"disambiguationData":[OSD([sQuery(id+"F7.wireOp",EDGE,"E8.left")])],"isStart":true})});
            var Q45;
            Q45=makeQuery(id+"F8.boolean.opBoolean","COPY",EDGE,{"derivedFrom":makeQuery(id+"F8.opExtrude","CAP_EDGE",EDGE,{"disambiguationData":[OSD([sQuery(id+"F7.wireOp",EDGE,"E7.left")])],"isStart":true})});
            var Q46;
            Q46=makeQuery(id+"F8.boolean.opBoolean","COPY",EDGE,{"derivedFrom":makeQuery(id+"F8.opExtrude","CAP_EDGE",EDGE,{"disambiguationData":[OSD([sQuery(id+"F7.wireOp",EDGE,"E7.right")])],"isStart":true})});
            var Q47;
            Q47=makeQuery(id+"F8.boolean.opBoolean","COPY",EDGE,{"derivedFrom":makeQuery(id+"F8.opExtrude","CAP_EDGE",EDGE,{"disambiguationData":[OSD([sQuery(id+"F7.wireOp",EDGE,"E8.right")])],"isStart":true})});
            fillet(context, id + "F15", {"entities" : qUnion([Q0, Q1, Q2, Q3, Q4, Q5, Q6, Q7, Q8, Q9, Q10, Q11, Q12, Q13, Q14, Q15, Q16, Q17, Q18, Q19, Q20, Q21, Q22, Q23, Q24, Q25, Q26, Q27, Q28, Q29, Q30, Q31, Q32, Q33, Q34, Q35, Q36, Q37, Q38, Q39, Q40, Q41, Q42, Q43, Q44, Q45, Q46, Q47]), "radius" : .3 * mm, "tangentPropagation" : true, "allowEdgeOverflow" : false});
        }
        {
            var Q0;
            Q0=makeQuery(id+"F10.boolean.opBoolean","MERGE",EDGE,{"derivedFrom":[makeQuery(id+"F5.boolean.opBoolean","COPY",EDGE,{"derivedFrom":makeQuery(id+"F5.opExtrude","CAP_EDGE",EDGE,{"disambiguationData":[OSD([sQuery(id+"F4.wireOp",EDGE,"E2.left")])],"isStart":false})}),makeQuery(id+"F10.opExtrude","SWEPT_EDGE",EDGE,{"disambiguationData":[OSD([sQuery(id+"F9.wireOp",EDGE,"E13"),sQuery(id+"F9.wireOp",EDGE,"E16")])]})]});
            fillet(context, id + "F16", {"entities" : qUnion([Q0]), "radius" : .5 * mm, "tangentPropagation" : true, "allowEdgeOverflow" : false});
        }
    });
